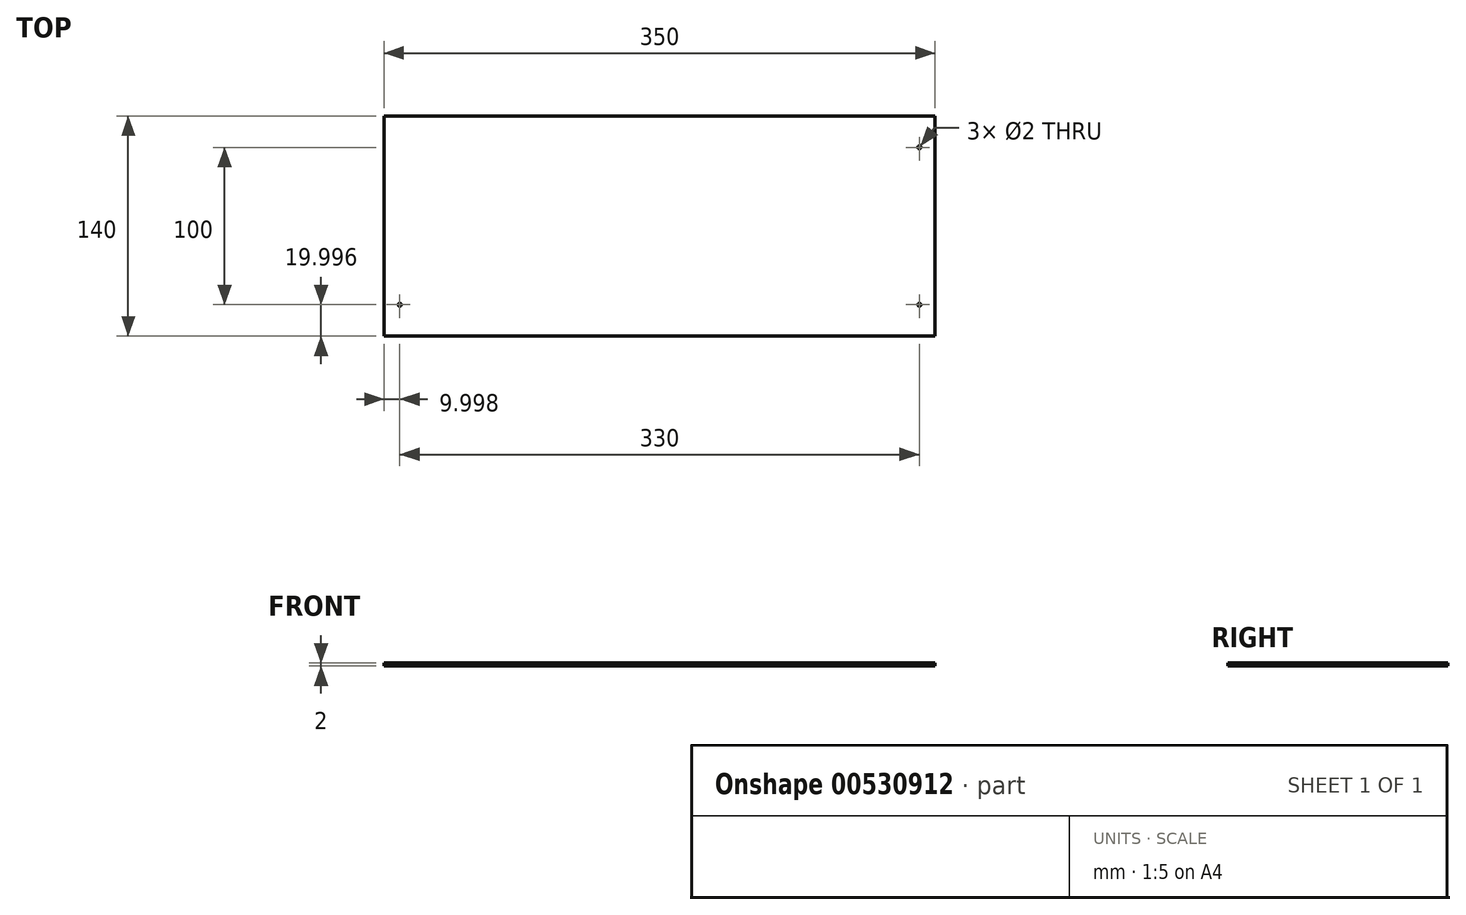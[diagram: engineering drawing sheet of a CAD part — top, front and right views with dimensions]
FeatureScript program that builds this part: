
annotation { "Feature Type Name" : "Feature", "Feature Type Description" : "" }
export const myFeature = defineFeature(function(context is Context, id is Id, definition is map)
    precondition{}
    {
        {
            var Q0;
            Q0=qCreatedBy(makeId("Top.planeOp"),FACE);
            var sketch = newSketch(context, id + "F0", { "sketchPlane" : qUnion([Q0])});
            skLineSegment(sketch, "E0.bottom", {"start": v(-146.31, 53.55) * mm, "end": v(203.69, 53.55) * mm});
            skLineSegment(sketch, "E0.top", {"start": v(-146.31, -86.45) * mm, "end": v(203.69, -86.45) * mm});
            skLineSegment(sketch, "E0.left", {"start": v(-146.31, 53.55) * mm, "end": v(-146.31, -86.45) * mm});
            skLineSegment(sketch, "E0.right", {"start": v(203.69, 53.55) * mm, "end": v(203.69, -86.45) * mm});
            skSolve(sketch);
        }
        {
            var Q0;
            Q0=makeQuery(id+"F0.imprint","IMPRINT",FACE,{"disambiguationData":[TD([[makeQuery(id+"F0.imprint","IMPRINT",EDGE,{"derivedFrom":sQuery(id+"F0.wireOp",EDGE,"E0.bottom")}),-1.0]])]});
            extrude(context, id + "F1", {"entities" : qUnion([Q0]), "depth" : 2 * mm, "offsetDistance" : 25.4 * mm});
        }
        {
            var Q0;
            Q0=makeQuery(id+"F1.opExtrude","CAP_FACE",FACE,{"disambiguationData":[OSD([sQuery(id+"F0.wireOp",EDGE,"E0.bottom"),sQuery(id+"F0.wireOp",EDGE,"E0.top"),sQuery(id+"F0.wireOp",EDGE,"E0.left"),sQuery(id+"F0.wireOp",EDGE,"E0.right")])],"isStart":false});
            var sketch = newSketch(context, id + "F2", { "sketchPlane" : qUnion([Q0])});
            skLineSegment(sketch, "E1", {"start": v(-146.31, -86.45) * mm, "end": v(-136.31, -86.45) * mm});
            skLineSegment(sketch, "E2", {"start": v(-136.31, -86.45) * mm, "end": v(-136.31, -66.45) * mm});
            skCircle(sketch, "E3", {"center": v(-136.31, -66.45) * mm, "radius": 1 * mm});
            skSolve(sketch);
        }
        {
            var Q0;
            Q0=makeQuery(id+"F2.imprint","IMPRINT",FACE,{"disambiguationData":[TD([[makeQuery(id+"F2.imprint","IMPRINT",EDGE,{"derivedFrom":sQuery(id+"F2.wireOp",EDGE,"E3")}),1.0]])]});
            extrude(context, id + "F3", {"entities" : qUnion([Q0]), "operationType" : NewBodyOperationType.REMOVE, "oppositeDirection" : true, "depth" : 25 * mm, "offsetDistance" : 25 * mm});
        }
        {
            var Q0;
            Q0=makeQuery(id+"F1.opExtrude","CAP_FACE",FACE,{"disambiguationData":[OSD([sQuery(id+"F0.wireOp",EDGE,"E0.bottom"),sQuery(id+"F0.wireOp",EDGE,"E0.top"),sQuery(id+"F0.wireOp",EDGE,"E0.left"),sQuery(id+"F0.wireOp",EDGE,"E0.right")])],"isStart":false});
            var sketch = newSketch(context, id + "F4", { "sketchPlane" : qUnion([Q0])});
            skLineSegment(sketch, "E4", {"start": v(203.69, 53.55) * mm, "end": v(193.69, 53.55) * mm});
            skLineSegment(sketch, "E5", {"start": v(193.69, 53.55) * mm, "end": v(193.69, 33.55) * mm});
            skLineSegment(sketch, "E6", {"start": v(203.69, -86.45) * mm, "end": v(193.69, -86.45) * mm});
            skLineSegment(sketch, "E7", {"start": v(193.69, -86.45) * mm, "end": v(193.69, -66.45) * mm});
            skCircle(sketch, "E8", {"center": v(193.69, 33.55) * mm, "radius": 1 * mm});
            skCircle(sketch, "E9", {"center": v(193.69, -66.45) * mm, "radius": 1 * mm});
            skSolve(sketch);
        }
        {
            var Q0;
            Q0=makeQuery(id+"F4.imprint","IMPRINT",FACE,{"disambiguationData":[TD([[makeQuery(id+"F4.imprint","IMPRINT",EDGE,{"derivedFrom":sQuery(id+"F4.wireOp",EDGE,"E8")}),1.0]])]});
            extrude(context, id + "F5", {"entities" : qUnion([Q0]), "operationType" : NewBodyOperationType.REMOVE, "oppositeDirection" : true, "depth" : 25 * mm, "offsetDistance" : 25 * mm});
        }
        {
            var Q0;
            Q0=makeQuery(id+"F1.opExtrude","CAP_FACE",FACE,{"disambiguationData":[OSD([sQuery(id+"F0.wireOp",EDGE,"E0.bottom"),sQuery(id+"F0.wireOp",EDGE,"E0.top"),sQuery(id+"F0.wireOp",EDGE,"E0.left"),sQuery(id+"F0.wireOp",EDGE,"E0.right")])],"isStart":false});
            var sketch = newSketch(context, id + "F6", { "sketchPlane" : qUnion([Q0])});
            skLineSegment(sketch, "E10", {"start": v(203.69, -86.45) * mm, "end": v(193.69, -86.45) * mm});
            skLineSegment(sketch, "E11", {"start": v(193.69, -86.45) * mm, "end": v(193.69, -66.45) * mm});
            skCircle(sketch, "E12", {"center": v(193.69, -66.45) * mm, "radius": 1 * mm});
            skSolve(sketch);
        }
        {
            var Q0;
            Q0=makeQuery(id+"F6.imprint","IMPRINT",FACE,{"disambiguationData":[TD([[makeQuery(id+"F6.imprint","IMPRINT",EDGE,{"derivedFrom":sQuery(id+"F6.wireOp",EDGE,"E12")}),1.0]])]});
            extrude(context, id + "F7", {"entities" : qUnion([Q0]), "operationType" : NewBodyOperationType.REMOVE, "oppositeDirection" : true, "depth" : 25 * mm, "offsetDistance" : 25 * mm});
        }
    });
